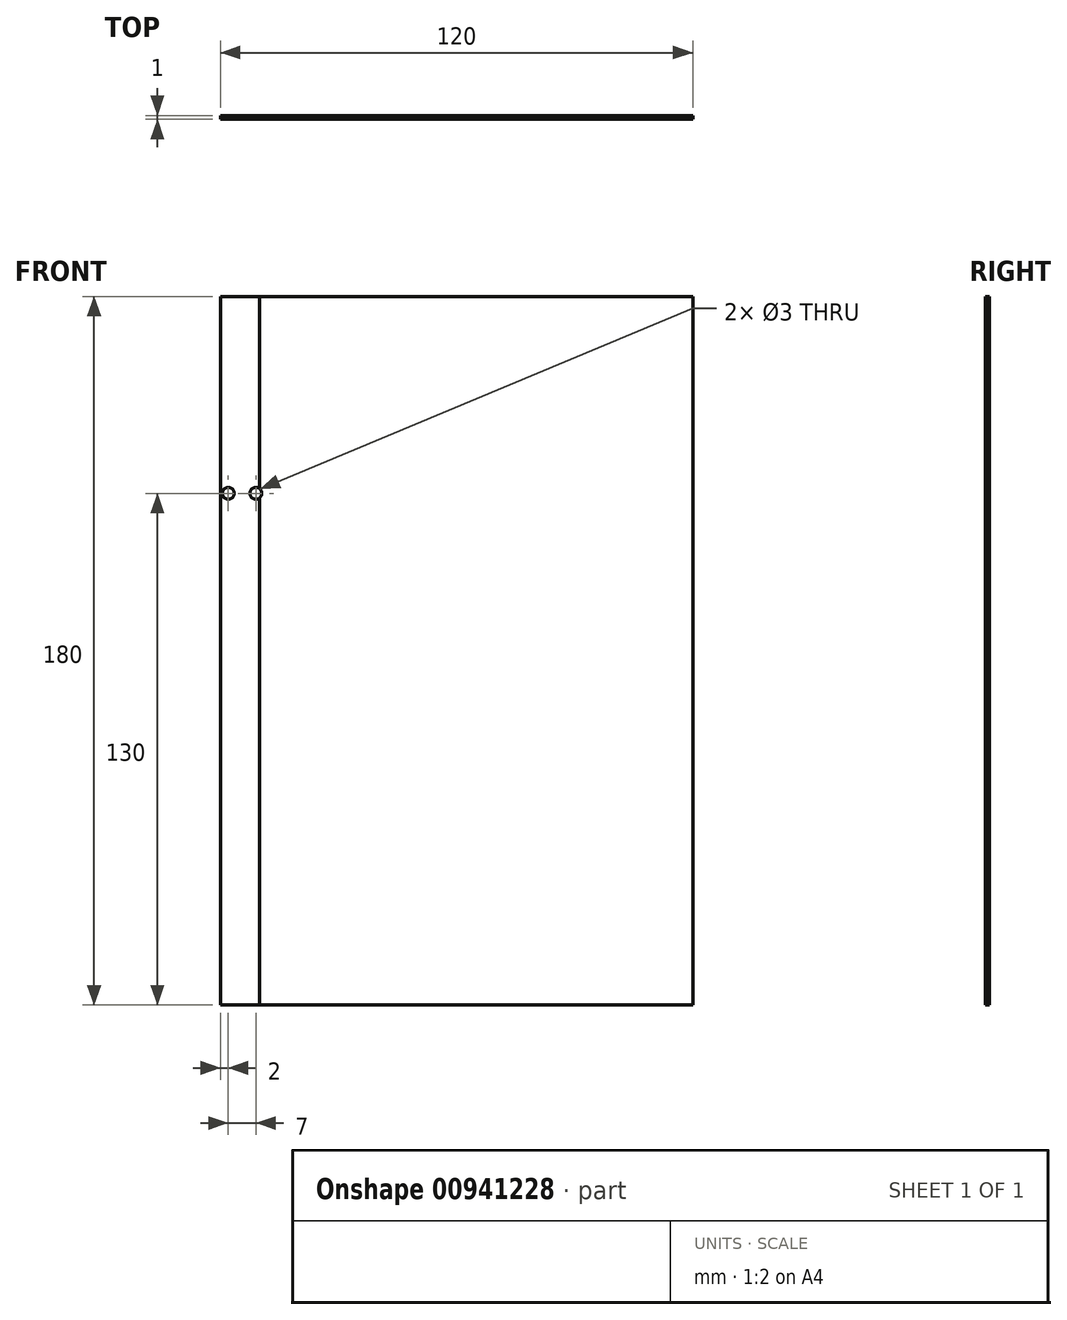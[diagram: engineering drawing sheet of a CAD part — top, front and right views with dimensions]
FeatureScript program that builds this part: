
annotation { "Feature Type Name" : "Feature", "Feature Type Description" : "" }
export const myFeature = defineFeature(function(context is Context, id is Id, definition is map)
    precondition{}
    {
        {
            var Q0;
            Q0=qCreatedBy(makeId("Top.planeOp"),FACE);
            var sketch = newSketch(context, id + "F0", { "sketchPlane" : qUnion([Q0])});
            skLineSegment(sketch, "E0.bottom", {"start": v(0, 0.5) * mm, "end": v(120, 0.5) * mm});
            skLineSegment(sketch, "E0.top", {"start": v(0, -0.5) * mm, "end": v(120, -0.5) * mm});
            skLineSegment(sketch, "E0.left", {"start": v(0, 0.5) * mm, "end": v(0, -0.5) * mm});
            skLineSegment(sketch, "E0.right", {"start": v(120, 0.5) * mm, "end": v(120, -0.5) * mm});
            skLineSegment(sketch, "E1", {"start": v(10, 0.5) * mm, "end": v(120, 0.05) * mm});
            skLineSegment(sketch, "E2", {"start": v(10, -0.5) * mm, "end": v(120, -0.05) * mm});
            skSolve(sketch);
        }
        {
            var Q0;
            {var subQ3=sQuery(id+"F0.wireOp",EDGE,"E0.left");Q0=makeQuery(id+"F0.imprint","IMPRINT",FACE,{"disambiguationData":[TD([[makeQuery(id+"F0.imprint","IMPRINT",EDGE,{"derivedFrom":subQ3}),1.0]])]});}
            extrude(context, id + "F1", {"entities" : qUnion([Q0]), "endBound" : BoundingType.SYMMETRIC, "depth" : 180 * mm, "offsetDistance" : 25 * mm});
        }
        {
            var Q0;
            {var subQ3=sQuery(id+"F0.wireOp",EDGE,"E1");Q0=makeQuery(id+"F0.imprint","IMPRINT",FACE,{"disambiguationData":[TD([[makeQuery(id+"F0.imprint","IMPRINT",EDGE,{"derivedFrom":subQ3}),1.0]])]});}
            var Q1;
            {var subQ3=sQuery(id+"F0.wireOp",EDGE,"E2");Q1=makeQuery(id+"F0.imprint","IMPRINT",FACE,{"disambiguationData":[TD([[makeQuery(id+"F0.imprint","IMPRINT",EDGE,{"derivedFrom":subQ3}),-1.0]])]});}
            extrude(context, id + "F2", {"entities" : qUnion([Q0, Q1]), "endBound" : BoundingType.SYMMETRIC, "depth" : 180 * mm, "offsetDistance" : 25 * mm});
        }
        {
            var Q0;
            Q0=qCreatedBy(makeId("Front.planeOp"),FACE);
            var sketch = newSketch(context, id + "F3", { "sketchPlane" : qUnion([Q0])});
            skCircle(sketch, "E3", {"center": v(2, 40) * mm, "radius": 1.5 * mm});
            skCircle(sketch, "E4", {"center": v(9, 40) * mm, "radius": 1.5 * mm});
            skSolve(sketch);
        }
        {
            var Q0;
            Q0 = qSketchRegion(id + "F3", true);
            extrude(context, id + "F4", {"entities" : qUnion([Q0]), "operationType" : NewBodyOperationType.REMOVE, "endBound" : BoundingType.SYMMETRIC, "oppositeDirection" : true, "depth" : 25 * mm, "offsetDistance" : 25 * mm});
        }
    });
